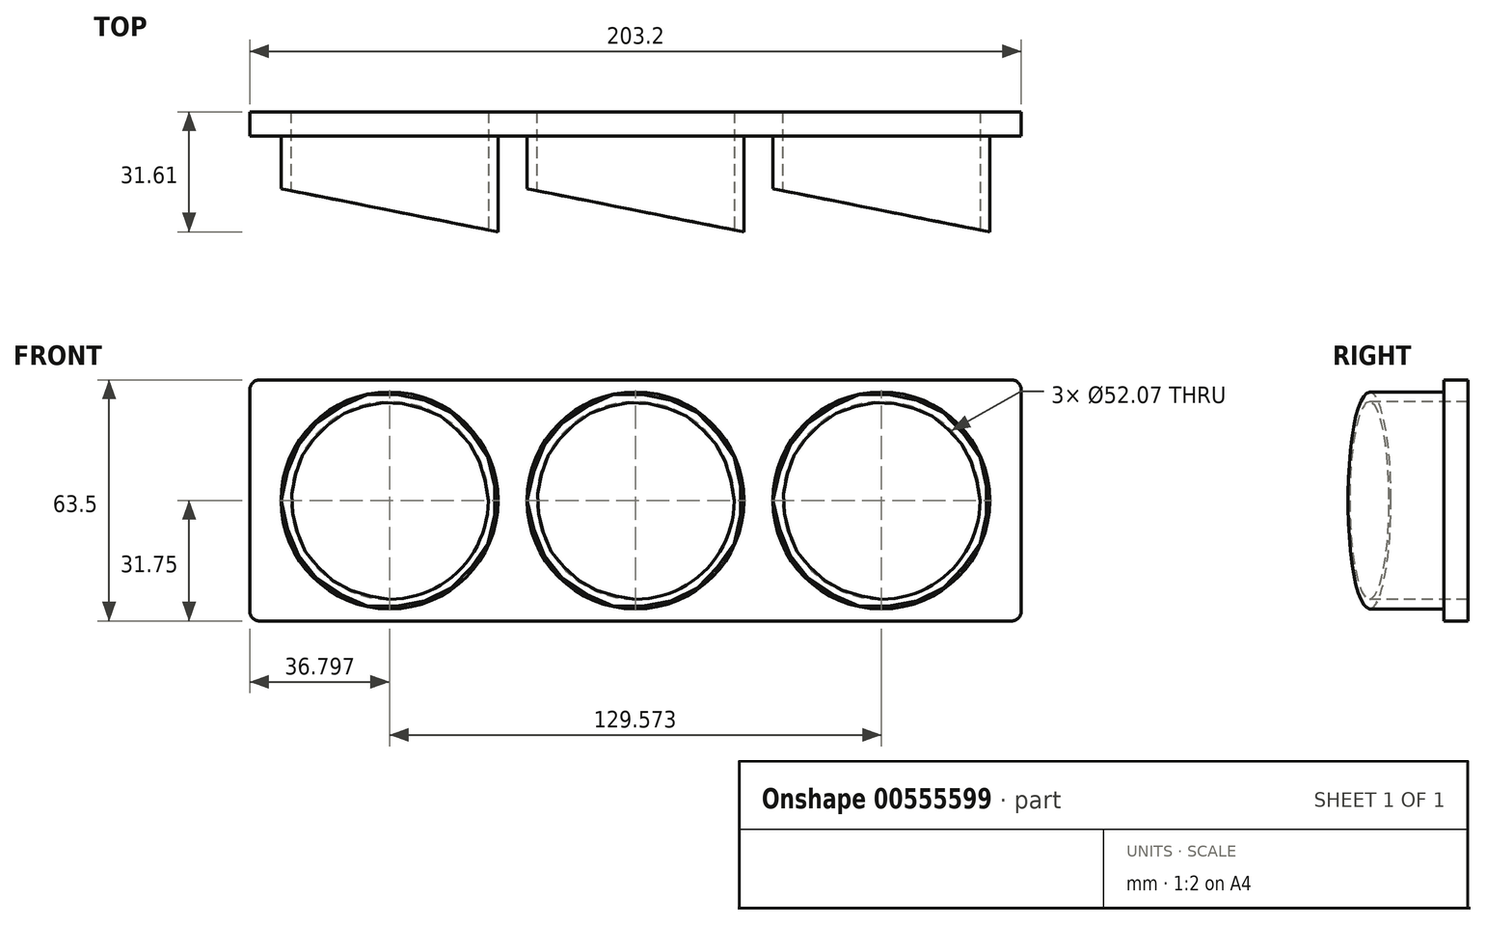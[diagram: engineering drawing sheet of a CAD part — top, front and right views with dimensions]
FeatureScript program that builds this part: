
annotation { "Feature Type Name" : "Feature", "Feature Type Description" : "" }
export const myFeature = defineFeature(function(context is Context, id is Id, definition is map)
    precondition{}
    {
        {
            var Q0;
            Q0=qCreatedBy(makeId("Front.planeOp"),FACE);
            var sketch = newSketch(context, id + "F0", { "sketchPlane" : qUnion([Q0])});
            skLineSegment(sketch, "E0.bottom", {"start": v(-101.6, 31.75) * mm, "end": v(101.6, 31.75) * mm});
            skLineSegment(sketch, "E0.top", {"start": v(-101.6, -31.75) * mm, "end": v(101.6, -31.75) * mm});
            skLineSegment(sketch, "E0.left", {"start": v(-101.6, 31.75) * mm, "end": v(-101.6, -31.75) * mm});
            skLineSegment(sketch, "E0.right", {"start": v(101.6, 31.75) * mm, "end": v(101.6, -31.75) * mm});
            skPoint(sketch, "E1.endSnap0", {"position": v(-101.6, 0) * mm});
            skPoint(sketch, "E2", {"position": v(-64.77, 0) * mm});
            skPoint(sketch, "E3", {"position": v(64.77, 0) * mm});
            skSolve(sketch);
        }
        {
            var Q0;
            Q0 = qSketchRegion(id + "F0", true);
            var Q1;
            Q1 = qSketchRegion(id + "FBQo1n0Ge6Jeqh7_0", true);
            extrude(context, id + "F1", {"entities" : qUnion([Q0, Q1]), "depth" : 6.35 * mm, "offsetDistance" : 25.4 * mm});
        }
        {
            var Q0;
            Q0=makeQuery(id+"F1.opExtrude","CAP_FACE",FACE,{"disambiguationData":[OSD([sQuery(id+"F0.wireOp",EDGE,"E0.bottom"),sQuery(id+"F0.wireOp",EDGE,"E0.top"),sQuery(id+"F0.wireOp",EDGE,"E0.left"),sQuery(id+"F0.wireOp",EDGE,"E0.right")])],"isStart":false});
            var sketch = newSketch(context, id + "F2", { "sketchPlane" : qUnion([Q0])});
            skCircle(sketch, "E4", {"center": v(0, 0) * mm, "radius": 26.04 * mm});
            skCircle(sketch, "E5", {"center": v(-64.8, 0) * mm, "radius": 26.04 * mm});
            skCircle(sketch, "E6", {"center": v(64.77, 0) * mm, "radius": 26.04 * mm});
            skSolve(sketch);
        }
        {
            var Q0;
            Q0=makeQuery(id+"F2.imprint","IMPRINT",FACE,{"disambiguationData":[TD([[makeQuery(id+"F2.imprint","IMPRINT",EDGE,{"derivedFrom":sQuery(id+"F2.wireOp",EDGE,"E5")}),1.0]])]});
            var Q1;
            Q1=makeQuery(id+"F2.imprint","IMPRINT",FACE,{"disambiguationData":[TD([[makeQuery(id+"F2.imprint","IMPRINT",EDGE,{"derivedFrom":sQuery(id+"F2.wireOp",EDGE,"E4")}),1.0]])]});
            var Q2;
            Q2=makeQuery(id+"F2.imprint","IMPRINT",FACE,{"disambiguationData":[TD([[makeQuery(id+"F2.imprint","IMPRINT",EDGE,{"derivedFrom":sQuery(id+"F2.wireOp",EDGE,"E6")}),1.0]])]});
            extrude(context, id + "F3", {"entities" : qUnion([Q0, Q1, Q2]), "operationType" : NewBodyOperationType.REMOVE, "oppositeDirection" : true, "depth" : 12.7 * mm, "offsetDistance" : 25.4 * mm});
        }
        {
            var Q0;
            Q0=makeQuery(id+"F2.imprint","IMPRINT",FACE,{"disambiguationData":[TD([[makeQuery(id+"F2.imprint","IMPRINT",EDGE,{"derivedFrom":sQuery(id+"F2.wireOp",EDGE,"E4")}),-1.0]])]});
            var sketch = newSketch(context, id + "F4", { "sketchPlane" : qUnion([Q0])});
            skCircle(sketch, "E7", {"center": v(-64.8, 0) * mm, "radius": 28.58 * mm});
            skCircle(sketch, "E8", {"center": v(0, 0) * mm, "radius": 28.58 * mm});
            skCircle(sketch, "E9", {"center": v(64.77, 0) * mm, "radius": 28.58 * mm});
            skSolve(sketch);
        }
        {
            var Q0;
            Q0=makeQuery(id+"F4.imprint","IMPRINT",FACE,{"disambiguationData":[TD([[makeQuery(id+"F4.imprint","IMPRINT",EDGE,{"derivedFrom":sQuery(id+"F4.wireOp",EDGE,"E7")}),1.0]])]});
            var Q1;
            Q1=makeQuery(id+"F4.imprint","IMPRINT",FACE,{"disambiguationData":[TD([[makeQuery(id+"F4.imprint","IMPRINT",EDGE,{"derivedFrom":sQuery(id+"F4.wireOp",EDGE,"E8")}),1.0]])]});
            var Q2;
            Q2=makeQuery(id+"F4.imprint","IMPRINT",FACE,{"disambiguationData":[TD([[makeQuery(id+"F4.imprint","IMPRINT",EDGE,{"derivedFrom":sQuery(id+"F4.wireOp",EDGE,"E9")}),1.0]])]});
            extrude(context, id + "F5", {"entities" : qUnion([Q0, Q1, Q2]), "operationType" : NewBodyOperationType.ADD, "depth" : 25.4 * mm, "offsetDistance" : 25.4 * mm});
        }
        {
            var Q0;
            Q0=qCreatedBy(makeId("Top.planeOp"),FACE);
            var sketch = newSketch(context, id + "F6", { "sketchPlane" : qUnion([Q0])});
            skLineSegment(sketch, "E10", {"start": v(35.62, -32) * mm, "end": v(95.3, -32) * mm});
            skLineSegment(sketch, "E11", {"start": v(95.3, -32) * mm, "end": v(35.62, -20.13) * mm});
            skLineSegment(sketch, "E12", {"start": v(35.62, -20.13) * mm, "end": v(35.62, -32) * mm});
            skLineSegment(sketch, "E13", {"start": v(95.3, -32) * mm, "end": v(95.3, -30.73) * mm, "construction": true});
            skLineSegment(sketch, "E14", {"start": v(95.3, -30.73) * mm, "end": v(93.35, -30.73) * mm, "construction": true});
            skLineSegment(sketch, "E15", {"start": v(-29.16, -32) * mm, "end": v(30.53, -32) * mm});
            skLineSegment(sketch, "E16", {"start": v(30.53, -32) * mm, "end": v(-29.16, -20.13) * mm});
            skLineSegment(sketch, "E17", {"start": v(-29.16, -20.13) * mm, "end": v(-29.16, -32) * mm});
            skLineSegment(sketch, "E18", {"start": v(30.53, -32) * mm, "end": v(30.53, -30.73) * mm, "construction": true});
            skLineSegment(sketch, "E19", {"start": v(30.53, -30.73) * mm, "end": v(28.58, -30.73) * mm, "construction": true});
            skLineSegment(sketch, "E20", {"start": v(-93.95, -32) * mm, "end": v(-34.26, -32) * mm});
            skLineSegment(sketch, "E21", {"start": v(-34.26, -32) * mm, "end": v(-93.95, -20.13) * mm});
            skLineSegment(sketch, "E22", {"start": v(-93.95, -20.13) * mm, "end": v(-93.95, -32) * mm});
            skLineSegment(sketch, "E23", {"start": v(-34.26, -32) * mm, "end": v(-34.26, -31.04) * mm, "construction": true});
            skLineSegment(sketch, "E24", {"start": v(-36.21, -31.04) * mm, "end": v(-34.26, -31.04) * mm, "construction": true});
            skSolve(sketch);
        }
        {
            var Q0;
            Q0 = qSketchRegion(id + "F6", true);
            extrude(context, id + "F7", {"entities" : qUnion([Q0]), "operationType" : NewBodyOperationType.REMOVE, "endBound" : BoundingType.SYMMETRIC, "oppositeDirection" : true, "depth" : 63.5 * mm, "offsetDistance" : 25.4 * mm});
        }
        {
            var Q0;
            Q0=makeQuery(id+"F1.opExtrude","SWEPT_EDGE",EDGE,{"disambiguationData":[OSD([sQuery(id+"F0.wireOp",EDGE,"E0.top"),sQuery(id+"F0.wireOp",EDGE,"E0.left")])]});
            var Q1;
            Q1=makeQuery(id+"F1.opExtrude","SWEPT_EDGE",EDGE,{"disambiguationData":[OSD([sQuery(id+"F0.wireOp",EDGE,"E0.bottom"),sQuery(id+"F0.wireOp",EDGE,"E0.left")])]});
            var Q2;
            Q2=makeQuery(id+"F1.opExtrude","SWEPT_EDGE",EDGE,{"disambiguationData":[OSD([sQuery(id+"F0.wireOp",EDGE,"E0.bottom"),sQuery(id+"F0.wireOp",EDGE,"E0.right")])]});
            var Q3;
            Q3=makeQuery(id+"F1.opExtrude","SWEPT_EDGE",EDGE,{"disambiguationData":[OSD([sQuery(id+"F0.wireOp",EDGE,"E0.top"),sQuery(id+"F0.wireOp",EDGE,"E0.right")])]});
            fillet(context, id + "F8", {"entities" : qUnion([Q0, Q1, Q2, Q3]), "radius" : 2.54 * mm, "tangentPropagation" : true, "allowEdgeOverflow" : false});
        }
    });
